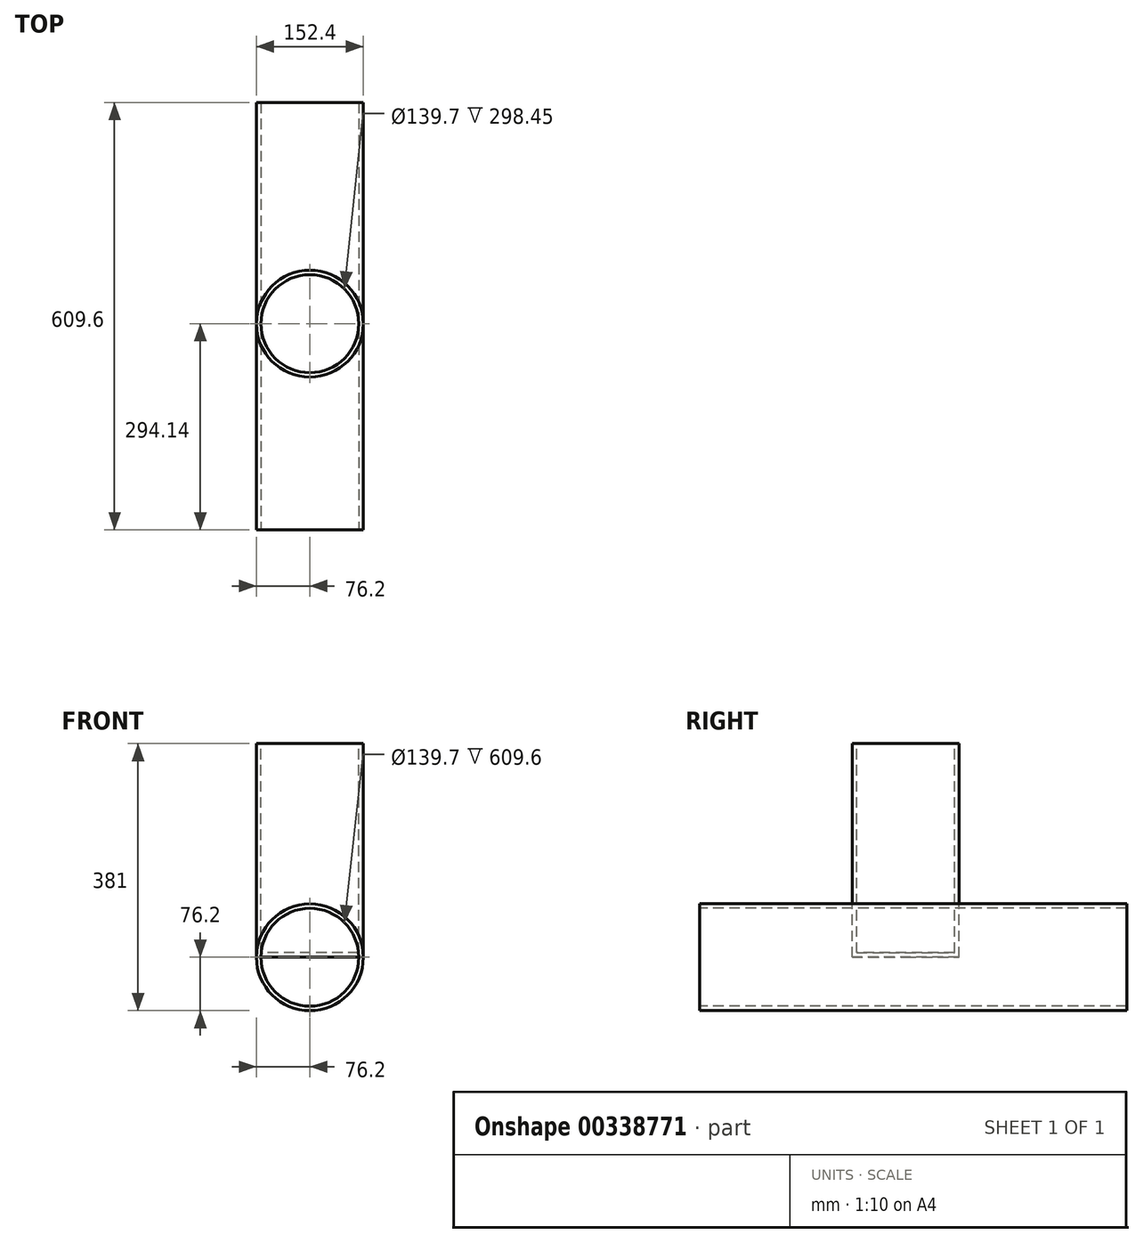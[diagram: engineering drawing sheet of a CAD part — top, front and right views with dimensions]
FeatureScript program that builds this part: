
annotation { "Feature Type Name" : "Feature", "Feature Type Description" : "" }
export const myFeature = defineFeature(function(context is Context, id is Id, definition is map)
    precondition{}
    {
        {
            var Q0;
            Q0=qCreatedBy(makeId("Right.planeOp"),FACE);
            var sketch = newSketch(context, id + "F0", { "sketchPlane" : qUnion([Q0])});
            skLineSegment(sketch, "E0", {"start": v(-294.14, 0) * mm, "end": v(315.46, 0) * mm});
            skLineSegment(sketch, "E1", {"start": v(0, 304.8) * mm, "end": v(0, 0) * mm});
            skSolve(sketch);
        }
        {
            var Q0;
            Q0=sQuery(id+"F0.wireOp",VERTEX,"E0.start");
            var Q1;
            Q1=qCreatedBy(makeId("Front.planeOp"),FACE);
            cPlane(context, id + "F1", {"entities" : qUnion([Q0, Q1]), "cplaneType" : CPlaneType.PLANE_POINT, "offset" : 320.04 * mm, "width" : 152.4 * mm, "height" : 152.4 * mm});
        }
        {
            var Q0;
            Q0=qCreatedBy(id+"F1.planeOp",FACE);
            var sketch = newSketch(context, id + "F2", { "sketchPlane" : qUnion([Q0])});
            skCircle(sketch, "E2", {"center": v(0, 0) * mm, "radius": 76.2 * mm});
            skSolve(sketch);
        }
        {
            var Q0;
            Q0=qCreatedBy(makeId("Top.planeOp"),FACE);
            var Q1;
            Q1=sQuery(id+"F0.wireOp",VERTEX,"E1.start");
            cPlane(context, id + "F3", {"entities" : qUnion([Q0, Q1]), "cplaneType" : CPlaneType.PLANE_POINT, "offset" : 25.4 * mm, "width" : 152.4 * mm, "height" : 152.4 * mm});
        }
        {
            var Q0;
            Q0=qCreatedBy(id+"F3.planeOp",FACE);
            var sketch = newSketch(context, id + "F4", { "sketchPlane" : qUnion([Q0])});
            skCircle(sketch, "E3", {"center": v(0, 0) * mm, "radius": 76.2 * mm});
            skSolve(sketch);
        }
        {
            var Q0;
            Q0=makeQuery(id+"F2.imprint","IMPRINT",FACE,{"disambiguationData":[TD([[makeQuery(id+"F2.imprint","IMPRINT",EDGE,{"derivedFrom":sQuery(id+"F2.wireOp",EDGE,"E2")}),1.0]])]});
            extrude(context, id + "F5", {"entities" : qUnion([Q0]), "oppositeDirection" : true, "depth" : 609.6 * mm});
        }
        {
            var Q0;
            Q0=makeQuery(id+"F4.imprint","IMPRINT",FACE,{"disambiguationData":[TD([[makeQuery(id+"F4.imprint","IMPRINT",EDGE,{"derivedFrom":sQuery(id+"F4.wireOp",EDGE,"E3")}),1.0]])]});
            extrude(context, id + "F6", {"entities" : qUnion([Q0]), "oppositeDirection" : true, "depth" : 304.8 * mm});
        }
        {
            var Q0;
            Q0=makeQuery(id+"F5.opExtrude","CAP_FACE",FACE,{"disambiguationData":[OSD([sQuery(id+"F2.wireOp",EDGE,"E2")])],"isStart":false});
            var Q1;
            Q1=makeQuery(id+"F6.opExtrude","CAP_FACE",FACE,{"disambiguationData":[OSD([sQuery(id+"F4.wireOp",EDGE,"E3")])],"isStart":true});
            var Q2;
            Q2=makeQuery(id+"F5.opExtrude","CAP_FACE",FACE,{"disambiguationData":[OSD([sQuery(id+"F2.wireOp",EDGE,"E2")])],"isStart":true});
            shell(context, id + "F7", {"entities" : qUnion([Q0, Q1, Q2]), "thickness" : 6.35 * mm});
        }
    });
